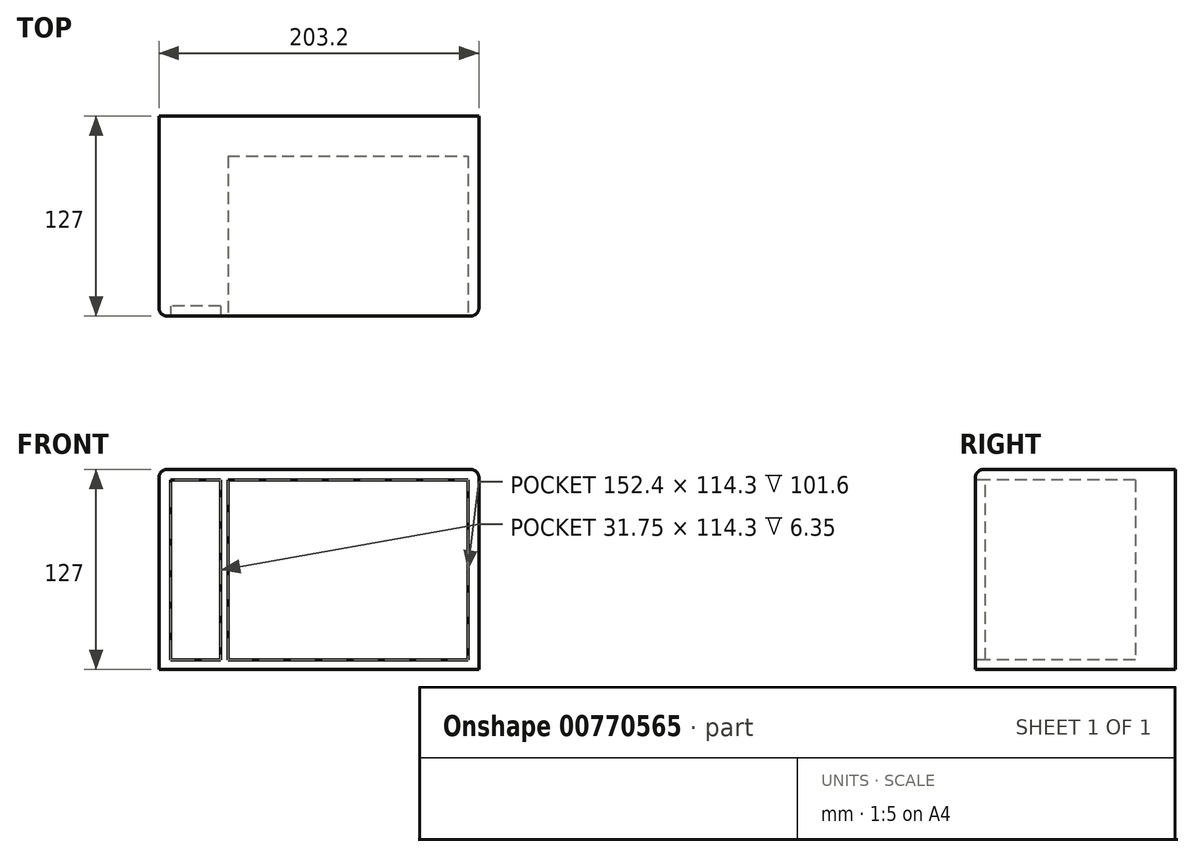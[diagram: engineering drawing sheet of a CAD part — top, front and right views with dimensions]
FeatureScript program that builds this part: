
annotation { "Feature Type Name" : "Feature", "Feature Type Description" : "" }
export const myFeature = defineFeature(function(context is Context, id is Id, definition is map)
    precondition{}
    {
        {
            var Q0;
            Q0=qCreatedBy(makeId("Top.planeOp"),FACE);
            var sketch = newSketch(context, id + "F0", { "sketchPlane" : qUnion([Q0])});
            skLineSegment(sketch, "E0.bottom", {"start": v(-63.2, 87.53) * mm, "end": v(140, 87.53) * mm});
            skLineSegment(sketch, "E0.top", {"start": v(-63.2, -39.47) * mm, "end": v(140, -39.47) * mm});
            skLineSegment(sketch, "E0.left", {"start": v(-63.2, 87.53) * mm, "end": v(-63.2, -39.47) * mm});
            skLineSegment(sketch, "E0.right", {"start": v(140, 87.53) * mm, "end": v(140, -39.47) * mm});
            skSolve(sketch);
        }
        {
            var Q0;
            Q0=makeQuery(id+"F0.imprint","IMPRINT",FACE,{"disambiguationData":[TD([[makeQuery(id+"F0.imprint","IMPRINT",EDGE,{"derivedFrom":sQuery(id+"F0.wireOp",EDGE,"E0.bottom")}),-1.0]])]});
            extrude(context, id + "F1", {"entities" : qUnion([Q0]), "depth" : 127 * mm, "offsetDistance" : 25.4 * mm});
        }
        {
            var Q0;
            Q0=makeQuery(id+"F1.opExtrude","CAP_EDGE",EDGE,{"disambiguationData":[OSD([sQuery(id+"F0.wireOp",EDGE,"E0.top")])],"isStart":false});
            var Q1;
            Q1=makeQuery(id+"F1.opExtrude","CAP_EDGE",EDGE,{"disambiguationData":[OSD([sQuery(id+"F0.wireOp",EDGE,"E0.left")])],"isStart":false});
            var Q2;
            Q2=makeQuery(id+"F1.opExtrude","CAP_EDGE",EDGE,{"disambiguationData":[OSD([sQuery(id+"F0.wireOp",EDGE,"E0.right")])],"isStart":false});
            var Q3;
            Q3=makeQuery(id+"F1.opExtrude","SWEPT_EDGE",EDGE,{"disambiguationData":[OSD([sQuery(id+"F0.wireOp",EDGE,"E0.top"),sQuery(id+"F0.wireOp",EDGE,"E0.right")])]});
            var Q4;
            Q4=makeQuery(id+"F1.opExtrude","SWEPT_EDGE",EDGE,{"disambiguationData":[OSD([sQuery(id+"F0.wireOp",EDGE,"E0.top"),sQuery(id+"F0.wireOp",EDGE,"E0.left")])]});
            fillet(context, id + "F2", {"entities" : qUnion([Q0, Q1, Q2, Q3, Q4]), "radius" : 5.08 * mm, "tangentPropagation" : true, "allowEdgeOverflow" : false});
        }
        {
            var Q0;
            Q0=makeQuery(id+"F1.opExtrude","SWEPT_FACE",FACE,{"disambiguationData":[OSD([sQuery(id+"F0.wireOp",EDGE,"E0.top")])]});
            var sketch = newSketch(context, id + "F3", { "sketchPlane" : qUnion([Q0])});
            skLineSegment(sketch, "E1.bottom", {"start": v(-19.36, 120.37) * mm, "end": v(133.04, 120.37) * mm});
            skLineSegment(sketch, "E1.top", {"start": v(-19.36, 6.07) * mm, "end": v(133.04, 6.07) * mm});
            skLineSegment(sketch, "E1.left", {"start": v(-19.36, 120.37) * mm, "end": v(-19.36, 6.07) * mm});
            skLineSegment(sketch, "E1.right", {"start": v(133.04, 120.37) * mm, "end": v(133.04, 6.07) * mm});
            skLineSegment(sketch, "E2.bottom", {"start": v(-24.05, 6.07) * mm, "end": v(-55.8, 6.07) * mm});
            skLineSegment(sketch, "E2.top", {"start": v(-24.05, 120.37) * mm, "end": v(-55.8, 120.37) * mm});
            skLineSegment(sketch, "E2.left", {"start": v(-24.05, 6.07) * mm, "end": v(-24.05, 120.37) * mm});
            skLineSegment(sketch, "E2.right", {"start": v(-55.8, 6.07) * mm, "end": v(-55.8, 120.37) * mm});
            skSolve(sketch);
        }
        {
            var Q0;
            Q0=makeQuery(id+"F3.imprint","IMPRINT",FACE,{"disambiguationData":[TD([[makeQuery(id+"F3.imprint","IMPRINT",EDGE,{"derivedFrom":sQuery(id+"F3.wireOp",EDGE,"E1.bottom")}),-1.0]])]});
            extrude(context, id + "F4", {"entities" : qUnion([Q0]), "operationType" : NewBodyOperationType.REMOVE, "oppositeDirection" : true, "depth" : 101.6 * mm, "offsetDistance" : 25.4 * mm});
        }
        {
            var Q0;
            Q0 = qSketchRegion(id + "F3", true);
            extrude(context, id + "F5", {"entities" : qUnion([Q0]), "operationType" : NewBodyOperationType.REMOVE, "oppositeDirection" : true, "depth" : 6.35 * mm, "offsetDistance" : 25.4 * mm});
        }
    });
